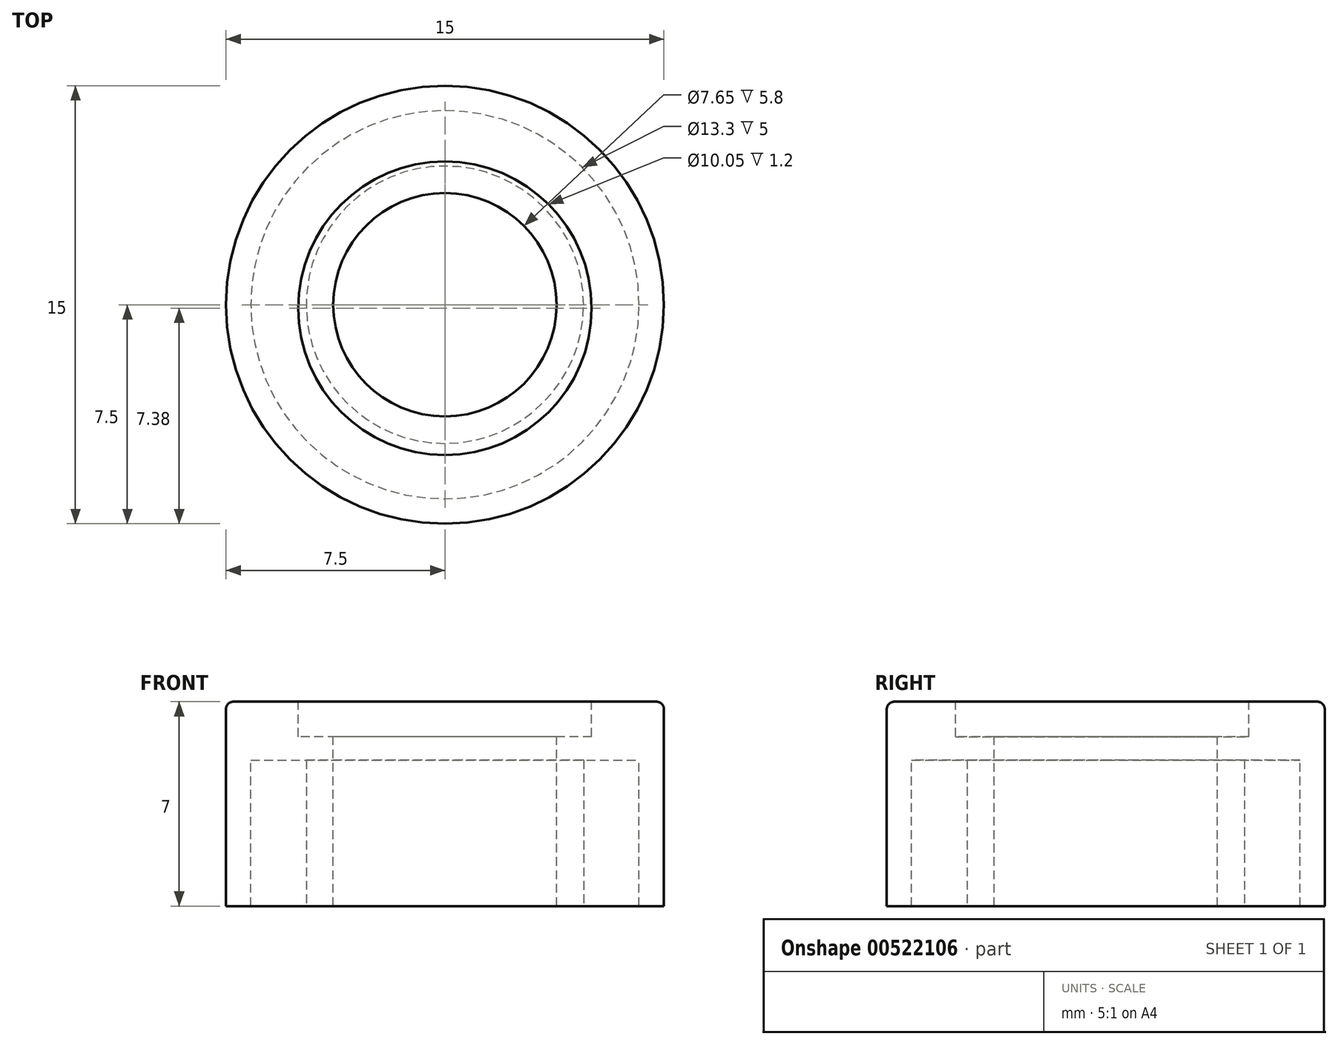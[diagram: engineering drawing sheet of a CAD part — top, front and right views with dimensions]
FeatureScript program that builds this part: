
annotation { "Feature Type Name" : "Feature", "Feature Type Description" : "" }
export const myFeature = defineFeature(function(context is Context, id is Id, definition is map)
    precondition{}
    {
        {
            var Q0;
            Q0=qCreatedBy(makeId("Top.planeOp"),FACE);
            var sketch = newSketch(context, id + "F0", { "sketchPlane" : qUnion([Q0])});
            skCircle(sketch, "E0", {"center": v(0, 0) * mm, "radius": 4.75 * mm});
            skSolve(sketch);
        }
        {
            var Q0;
            Q0 = qSketchRegion(id + "F0", true);
            extrude(context, id + "F1", {"entities" : qUnion([Q0]), "depth" : 5 * mm, "offsetDistance" : 25 * mm});
        }
        {
            var Q0;
            Q0=makeQuery(id+"F1.opExtrude","CAP_FACE",FACE,{"disambiguationData":[OSD([sQuery(id+"F0.wireOp",EDGE,"E0")])],"isStart":false});
            var sketch = newSketch(context, id + "F2", { "sketchPlane" : qUnion([Q0])});
            skCircle(sketch, "E1", {"center": v(0, 0) * mm, "radius": 7.5 * mm});
            skSolve(sketch);
        }
        {
            var Q0;
            Q0 = qSketchRegion(id + "F2", true);
            extrude(context, id + "F3", {"entities" : qUnion([Q0]), "operationType" : NewBodyOperationType.ADD, "depth" : 2 * mm, "offsetDistance" : 25 * mm});
        }
        {
            var Q0;
            Q0=makeQuery(id+"F3.opExtrude","CAP_FACE",FACE,{"disambiguationData":[OSD([sQuery(id+"F2.wireOp",EDGE,"E1")])],"isStart":false});
            var sketch = newSketch(context, id + "F4", { "sketchPlane" : qUnion([Q0])});
            skCircle(sketch, "E2", {"center": v(0, 0) * mm, "radius": 3.82 * mm});
            skSolve(sketch);
        }
        {
            var Q0;
            Q0 = qSketchRegion(id + "F4", true);
            extrude(context, id + "F5", {"entities" : qUnion([Q0]), "operationType" : NewBodyOperationType.REMOVE, "oppositeDirection" : true, "depth" : 25 * mm, "offsetDistance" : 25 * mm});
        }
        {
            var Q0;
            Q0=makeQuery(id+"F3.opExtrude","CAP_EDGE",EDGE,{"disambiguationData":[OSD([sQuery(id+"F2.wireOp",EDGE,"E1")])],"isStart":false});
            fillet(context, id + "F6", {"entities" : qUnion([Q0]), "radius" : .25 * mm, "tangentPropagation" : true, "allowEdgeOverflow" : false});
        }
        {
            var Q0;
            Q0=makeQuery(id+"F3.opExtrude","CAP_FACE",FACE,{"disambiguationData":[OSD([sQuery(id+"F2.wireOp",EDGE,"E1")])],"isStart":true});
            var sketch = newSketch(context, id + "F7", { "sketchPlane" : qUnion([Q0])});
            skLineSegment(sketch, "E3", {"start": v(-4.75, 0) * mm, "end": v(-6.65, 0) * mm, "construction": true});
            skCircle(sketch, "E4", {"center": v(0, 0) * mm, "radius": 6.65 * mm});
            skSolve(sketch);
        }
        {
            var Q0;
            Q0=makeQuery(id+"F7.imprint","IMPRINT",FACE,{"disambiguationData":[TD([[makeQuery(id+"F7.imprint","IMPRINT",EDGE,{"derivedFrom":sQuery(id+"F7.wireOp",EDGE,"E4")}),-1.0]])]});
            extrude(context, id + "F8", {"entities" : qUnion([Q0]), "operationType" : NewBodyOperationType.ADD, "depth" : 5 * mm, "offsetDistance" : 25 * mm});
        }
        {
            var Q0;
            Q0=makeQuery(id+"F3.opExtrude","CAP_FACE",FACE,{"disambiguationData":[OSD([sQuery(id+"F2.wireOp",EDGE,"E1")])],"isStart":false});
            var sketch = newSketch(context, id + "F9", { "sketchPlane" : qUnion([Q0])});
            skLineSegment(sketch, "E5", {"start": v(-3.82, 0) * mm, "end": v(-5.03, 0) * mm, "construction": true});
            skCircle(sketch, "E6", {"center": v(0, -0.12) * mm, "radius": 5.03 * mm});
            skSolve(sketch);
        }
        {
            var Q0;
            Q0=makeQuery(id+"F9.imprint","IMPRINT",FACE,{"disambiguationData":[TD([[makeQuery(id+"F9.imprint","IMPRINT",EDGE,{"derivedFrom":sQuery(id+"F9.wireOp",EDGE,"E6")}),1.0]])]});
            extrude(context, id + "F10", {"entities" : qUnion([Q0]), "operationType" : NewBodyOperationType.REMOVE, "oppositeDirection" : true, "depth" : 1.2 * mm, "offsetDistance" : 25 * mm});
        }
    });
